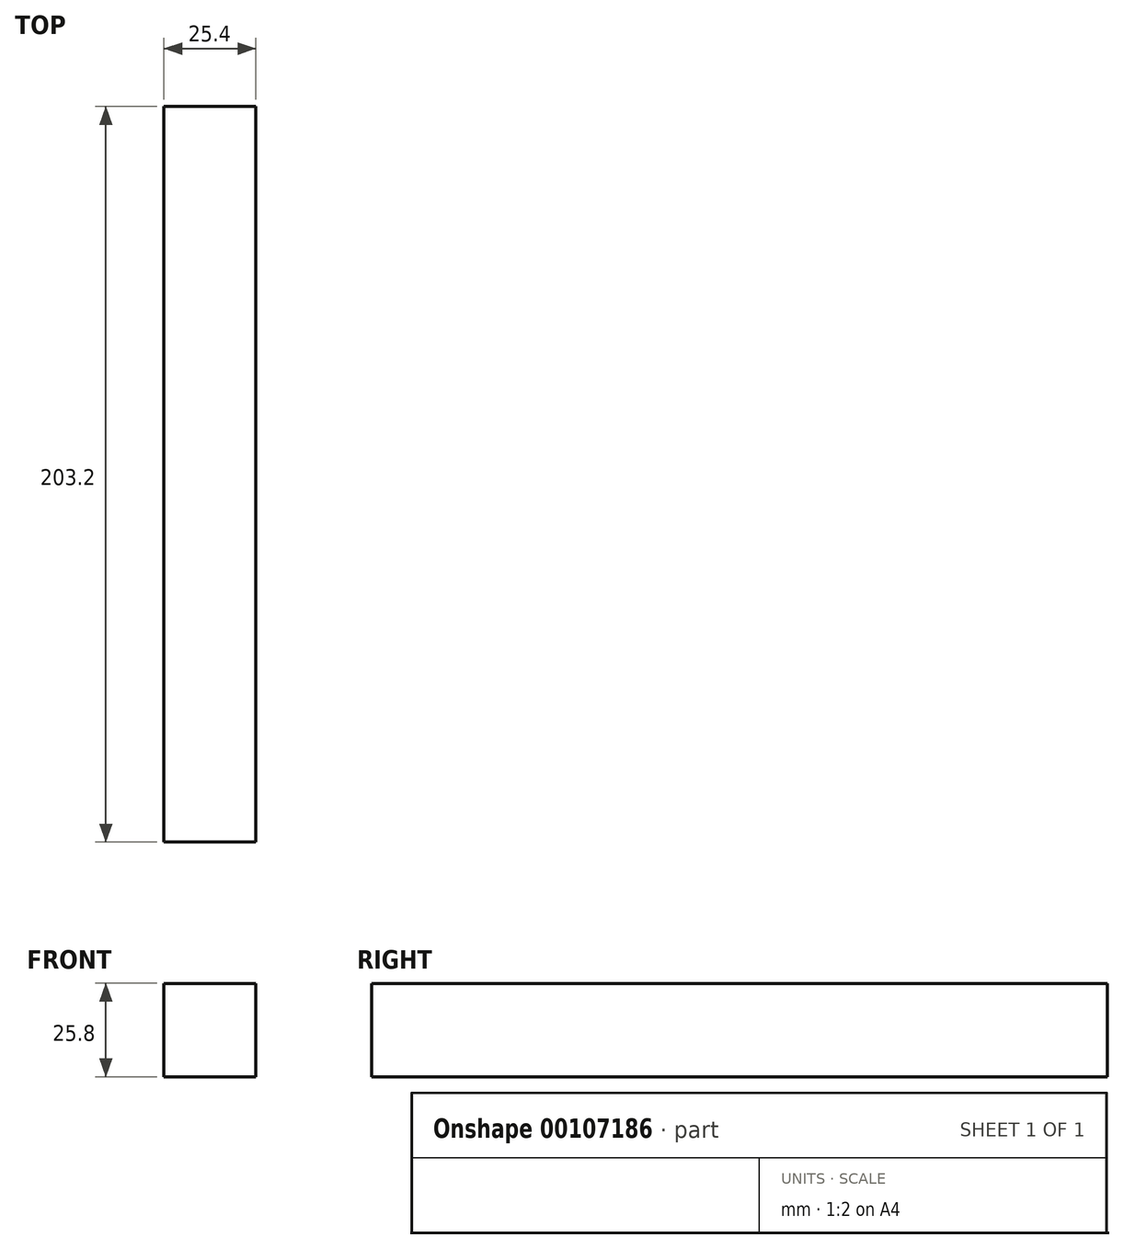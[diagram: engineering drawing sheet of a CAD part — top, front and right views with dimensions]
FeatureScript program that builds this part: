
annotation { "Feature Type Name" : "Feature", "Feature Type Description" : "" }
export const myFeature = defineFeature(function(context is Context, id is Id, definition is map)
    precondition{}
    {
        {
            var Q0;
            Q0=qCreatedBy(makeId("Right.planeOp"),FACE);
            var sketch = newSketch(context, id + "F0", { "sketchPlane" : qUnion([Q0])});
            skLineSegment(sketch, "E0.bottom", {"start": v(-101.6, 12.9) * mm, "end": v(101.6, 12.9) * mm});
            skLineSegment(sketch, "E0.top", {"start": v(-101.6, -12.9) * mm, "end": v(101.6, -12.9) * mm});
            skLineSegment(sketch, "E0.left", {"start": v(-101.6, 12.9) * mm, "end": v(-101.6, -12.9) * mm});
            skLineSegment(sketch, "E0.right", {"start": v(101.6, 12.9) * mm, "end": v(101.6, -12.9) * mm});
            skPoint(sketch, "E0.middle", {"position": v(0, 0) * mm});
            skSolve(sketch);
        }
        {
            var Q0;
            Q0=makeQuery(id+"F0.imprint","IMPRINT",FACE,{"disambiguationData":[TD([[makeQuery(id+"F0.imprint","IMPRINT",EDGE,{"derivedFrom":sQuery(id+"F0.wireOp",EDGE,"E0.bottom")}),-1.0]])]});
            extrude(context, id + "F1", {"entities" : qUnion([Q0]), "depth" : 25.4 * mm});
        }
    });
